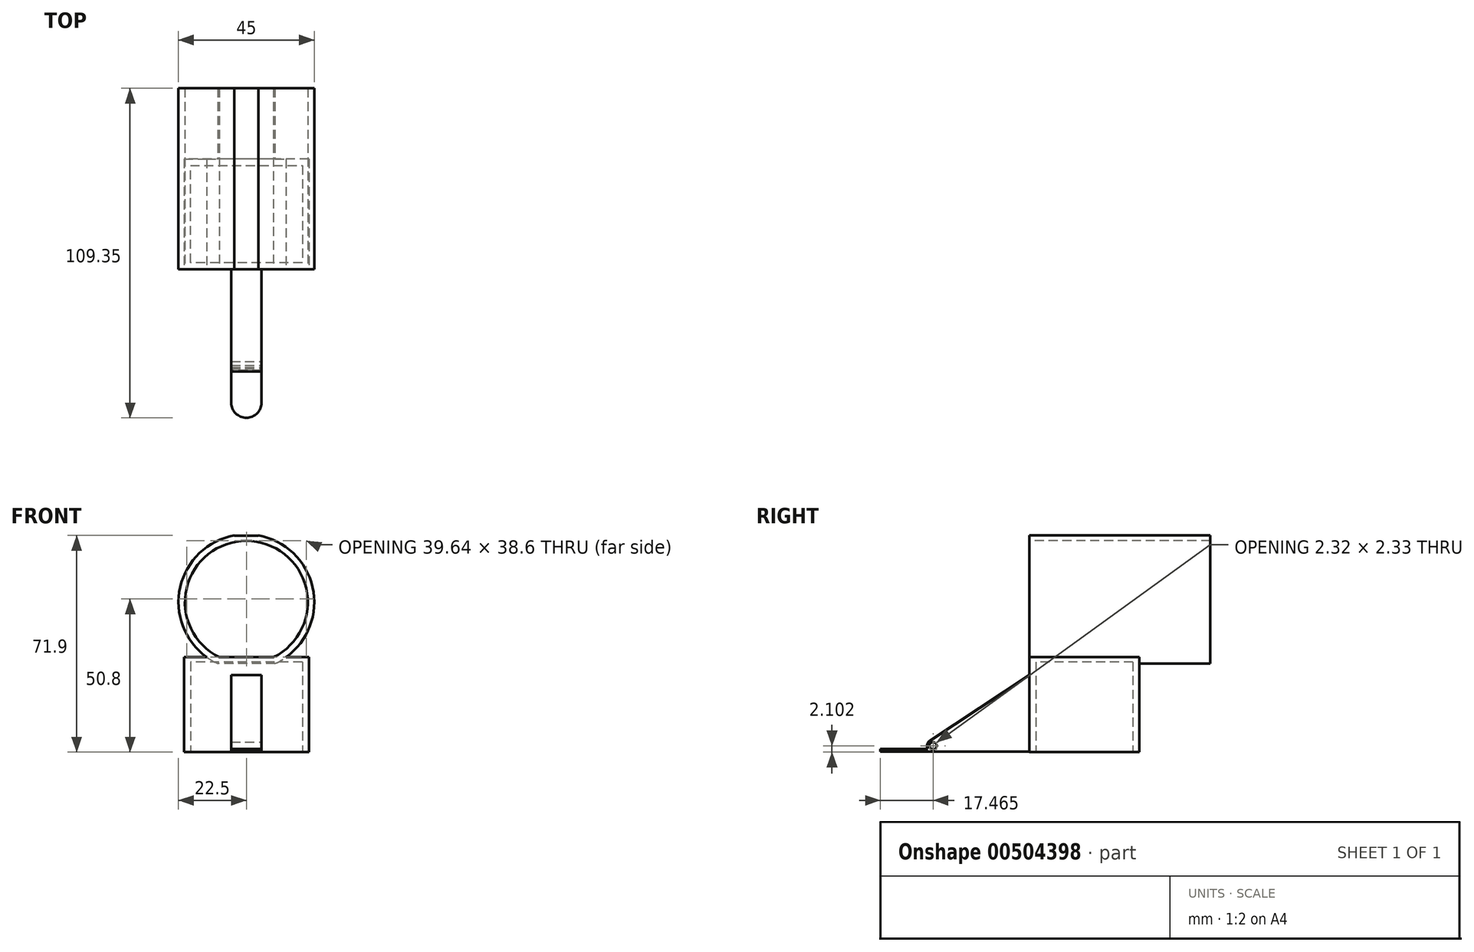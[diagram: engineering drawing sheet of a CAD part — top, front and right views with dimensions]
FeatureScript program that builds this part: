
annotation { "Feature Type Name" : "Feature", "Feature Type Description" : "" }
export const myFeature = defineFeature(function(context is Context, id is Id, definition is map)
    precondition{}
    {
        {
            var Q0;
            Q0=qCreatedBy(makeId("Front.planeOp"),FACE);
            var sketch = newSketch(context, id + "F0", { "sketchPlane" : qUnion([Q0])});
            skArc(sketch, "E0", {"start": v(9.5, -20.4) * mm, "mid": v(0, 22.5) * mm, "end": v(-9.5, -20.4) * mm});
            skCircle(sketch, "E1", {"center": v(0, 29) * mm, "radius": 5.15 * mm});
            skLineSegment(sketch, "E2.bottom", {"start": v(20.7, -18.25) * mm, "end": v(15.43, -18.25) * mm});
            skLineSegment(sketch, "E2.top", {"start": v(20.7, -49.75) * mm, "end": v(-20.7, -49.75) * mm});
            skLineSegment(sketch, "E2.left", {"start": v(20.7, -18.25) * mm, "end": v(20.7, -49.75) * mm});
            skLineSegment(sketch, "E2.right", {"start": v(-20.7, -18.25) * mm, "end": v(-20.7, -49.75) * mm});
            skPoint(sketch, "E2.middle", {"position": v(0, -34) * mm});
            skLineSegment(sketch, "E3.bottom", {"start": v(3.95, 27.9) * mm, "end": v(-3.95, 27.9) * mm});
            skLineSegment(sketch, "E3.top", {"start": v(3.95, 22.1) * mm, "end": v(-3.95, 22.1) * mm});
            skLineSegment(sketch, "E3.left", {"start": v(3.95, 27.9) * mm, "end": v(3.95, 22.1) * mm});
            skLineSegment(sketch, "E3.right", {"start": v(-3.95, 27.9) * mm, "end": v(-3.95, 22.1) * mm});
            skPoint(sketch, "E3.middle", {"position": v(0, 25) * mm});
            skLineSegment(sketch, "E4.0", {"start": v(-18.55, -20.4) * mm, "end": v(-18.55, -47.6) * mm});
            skLineSegment(sketch, "E4.1", {"start": v(18.55, -20.4) * mm, "end": v(-18.55, -20.4) * mm});
            skLineSegment(sketch, "E4.2", {"start": v(18.55, -20.4) * mm, "end": v(18.55, -47.6) * mm});
            skLineSegment(sketch, "E4.3", {"start": v(18.55, -47.6) * mm, "end": v(-18.55, -47.6) * mm});
            skArc(sketch, "E5.0", {"start": v(9, -18.25) * mm, "mid": v(0, 20.35) * mm, "end": v(-9, -18.25) * mm});
            skArc(sketch, "E6.0", {"start": v(15.43, -18.25) * mm, "mid": v(0, 23.9) * mm, "end": v(-15.43, -18.25) * mm});
            skLineSegment(sketch, "E7.0", {"start": v(-1.55, 27.9) * mm, "end": v(-1.55, 22.1) * mm});
            skLineSegment(sketch, "E8.0", {"start": v(1.55, 27.9) * mm, "end": v(1.55, 22.1) * mm});
            skCircle(sketch, "E9", {"center": v(0, 0) * mm, "radius": 18.25 * mm});
            skLineSegment(sketch, "E10.trimOffspring", {"start": v(-15.43, -18.25) * mm, "end": v(-20.7, -18.25) * mm});
            skLineSegment(sketch, "E11", {"start": v(-9, -18.25) * mm, "end": v(9, -18.25) * mm});
            skLineSegment(sketch, "E12", {"start": v(-15.43, -18.25) * mm, "end": v(-13.16, -18.25) * mm});
            skLineSegment(sketch, "E13", {"start": v(15.43, -18.25) * mm, "end": v(13.16, -18.25) * mm});
            skSolve(sketch);
        }
        {
            var Q0;
            Q0=sQuery(id+"F0.wireOp",EDGE,"E1");
            extrude(context, id + "F1", {"bodyType" : ToolBodyType.SURFACE, "surfaceEntities" : qUnion([Q0]), "oppositeDirection" : true, "depth" : 60 * mm});
        }
        {
            var Q0;
            {var subQ14=sQuery(id+"F0.wireOp",EDGE,"E5.0");Q0=makeQuery(id+"F0.imprint","IMPRINT",FACE,{"disambiguationData":[TD([[makeQuery(id+"F0.imprint","IMPRINT",EDGE,{"derivedFrom":subQ14}),-1.0]])]});}
            extrude(context, id + "F2", {"entities" : qUnion([Q0]), "oppositeDirection" : true, "depth" : 60 * mm});
        }
        {
            var Q0;
            {var subQ3=sQuery(id+"F0.wireOp",EDGE,"E4.0");Q0=makeQuery(id+"F0.imprint","IMPRINT",FACE,{"disambiguationData":[TD([[makeQuery(id+"F0.imprint","IMPRINT",EDGE,{"derivedFrom":subQ3}),1.0]])]});}
            var Q1;
            Q1=makeQuery(id+"F0.imprint","IMPRINT",FACE,{"disambiguationData":[TD([[makeQuery(id+"F0.imprint","IMPRINT",EDGE,{"derivedFrom":sQuery(id+"F0.wireOp",EDGE,"E2.bottom")}),1.0]])]});
            extrude(context, id + "F3", {"entities" : qUnion([Q0, Q1]), "operationType" : NewBodyOperationType.ADD, "oppositeDirection" : true, "depth" : 36.5 * mm});
        }
        {
            var Q0;
            Q0=makeQuery(id+"F3.opExtrude","SWEPT_FACE",FACE,{"disambiguationData":[OSD([sQuery(id+"F0.wireOp",EDGE,"E2.top")])]});
            var sketch = newSketch(context, id + "F4", { "sketchPlane" : qUnion([Q0])});
            skLineSegment(sketch, "E14.0", {"start": v(18.55, -2.15) * mm, "end": v(-18.55, -2.15) * mm});
            skLineSegment(sketch, "E14.1", {"start": v(18.55, -34.35) * mm, "end": v(18.55, -2.15) * mm});
            skLineSegment(sketch, "E14.2", {"start": v(-18.55, -34.35) * mm, "end": v(18.55, -34.35) * mm});
            skLineSegment(sketch, "E14.3", {"start": v(-18.55, -2.15) * mm, "end": v(-18.55, -34.35) * mm});
            skSolve(sketch);
        }
        {
            var Q0;
            Q0=makeQuery(id+"F4.imprint","IMPRINT",FACE,{"disambiguationData":[TD([[makeQuery(id+"F4.imprint","IMPRINT",EDGE,{"derivedFrom":sQuery(id+"F4.wireOp",EDGE,"E14.0")}),1.0]])]});
            extrude(context, id + "F5", {"entities" : qUnion([Q0]), "operationType" : NewBodyOperationType.REMOVE, "oppositeDirection" : true, "depth" : 29.86 * mm});
        }
        {
            var Q0;
            Q0=qCreatedBy(makeId("Right.planeOp"),FACE);
            var sketch = newSketch(context, id + "F6", { "sketchPlane" : qUnion([Q0])});
            skLineSegment(sketch, "E15.bottom", {"start": v(0, -49.62) * mm, "end": v(-31.9, -49.62) * mm});
            skLineSegment(sketch, "E15.left", {"start": v(0, -49.62) * mm, "end": v(0, -24.13) * mm});
            skLineSegment(sketch, "E16", {"start": v(0, -24.13) * mm, "end": v(-33, -45.96) * mm});
            skPoint(sketch, "E17.visualSharp", {"position": v(-38.55, -49.62) * mm});
            skArc(sketch, "E17.filletArc", {"start": v(-33, -45.96) * mm, "mid": v(-33.82, -48.2) * mm, "end": v(-31.9, -49.62) * mm});
            skSolve(sketch);
        }
        {
            var Q0;
            Q0 = qSketchRegion(id + "F6", true);
            extrude(context, id + "F7", {"entities" : qUnion([Q0]), "endBound" : BoundingType.SYMMETRIC, "depth" : 10 * mm, "offsetDistance" : 25 * mm});
        }
        {
            var Q0;
            Q0=makeQuery(id+"F7.opExtrude","CAP_FACE",FACE,{"disambiguationData":[OSD([sQuery(id+"F6.wireOp",EDGE,"E15.bottom"),sQuery(id+"F6.wireOp",EDGE,"E15.left"),sQuery(id+"F6.wireOp",EDGE,"E16"),sQuery(id+"F6.wireOp",EDGE,"E17.filletArc")])],"isStart":false});
            var sketch = newSketch(context, id + "F8", { "sketchPlane" : qUnion([Q0])});
            skCircle(sketch, "E18", {"center": v(-31.9, -47.62) * mm, "radius": 1.2 * mm});
            skSolve(sketch);
        }
        {
            var Q0;
            Q0 = qSketchRegion(id + "F8", true);
            extrude(context, id + "F9", {"entities" : qUnion([Q0]), "operationType" : NewBodyOperationType.REMOVE, "endBound" : BoundingType.THROUGH_ALL, "oppositeDirection" : true, "depth" : 25 * mm, "offsetDistance" : 25 * mm});
        }
        {
            var Q0;
            Q0=makeQuery(id+"F7.opExtrude","SWEPT_FACE",FACE,{"disambiguationData":[OSD([sQuery(id+"F6.wireOp",EDGE,"E15.bottom")])]});
            var sketch = newSketch(context, id + "F10", { "sketchPlane" : qUnion([Q0])});
            skLineSegment(sketch, "E19.bottom", {"start": v(-5, 0) * mm, "end": v(5, 0) * mm});
            skArc(sketch, "E20", {"start": v(5, 44.35) * mm, "mid": v(0, 49.35) * mm, "end": v(-5, 44.35) * mm});
            skLineSegment(sketch, "E21.top", {"start": v(-5, 31.9) * mm, "end": v(5, 31.9) * mm});
            skLineSegment(sketch, "E21.left", {"start": v(-5, 44.35) * mm, "end": v(-5, 31.9) * mm});
            skLineSegment(sketch, "E21.right", {"start": v(5, 44.35) * mm, "end": v(5, 31.9) * mm});
            skSolve(sketch);
        }
        {
            var Q0;
            Q0=makeQuery(id+"F10.imprint","IMPRINT",FACE,{"disambiguationData":[TD([[makeQuery(id+"F10.imprint","IMPRINT",EDGE,{"derivedFrom":sQuery(id+"F10.wireOp",EDGE,"E20")}),1.0]])]});
            extrude(context, id + "F11", {"entities" : qUnion([Q0]), "operationType" : NewBodyOperationType.ADD, "oppositeDirection" : true, "depth" : 1 * mm, "offsetDistance" : 25 * mm});
        }
    });
